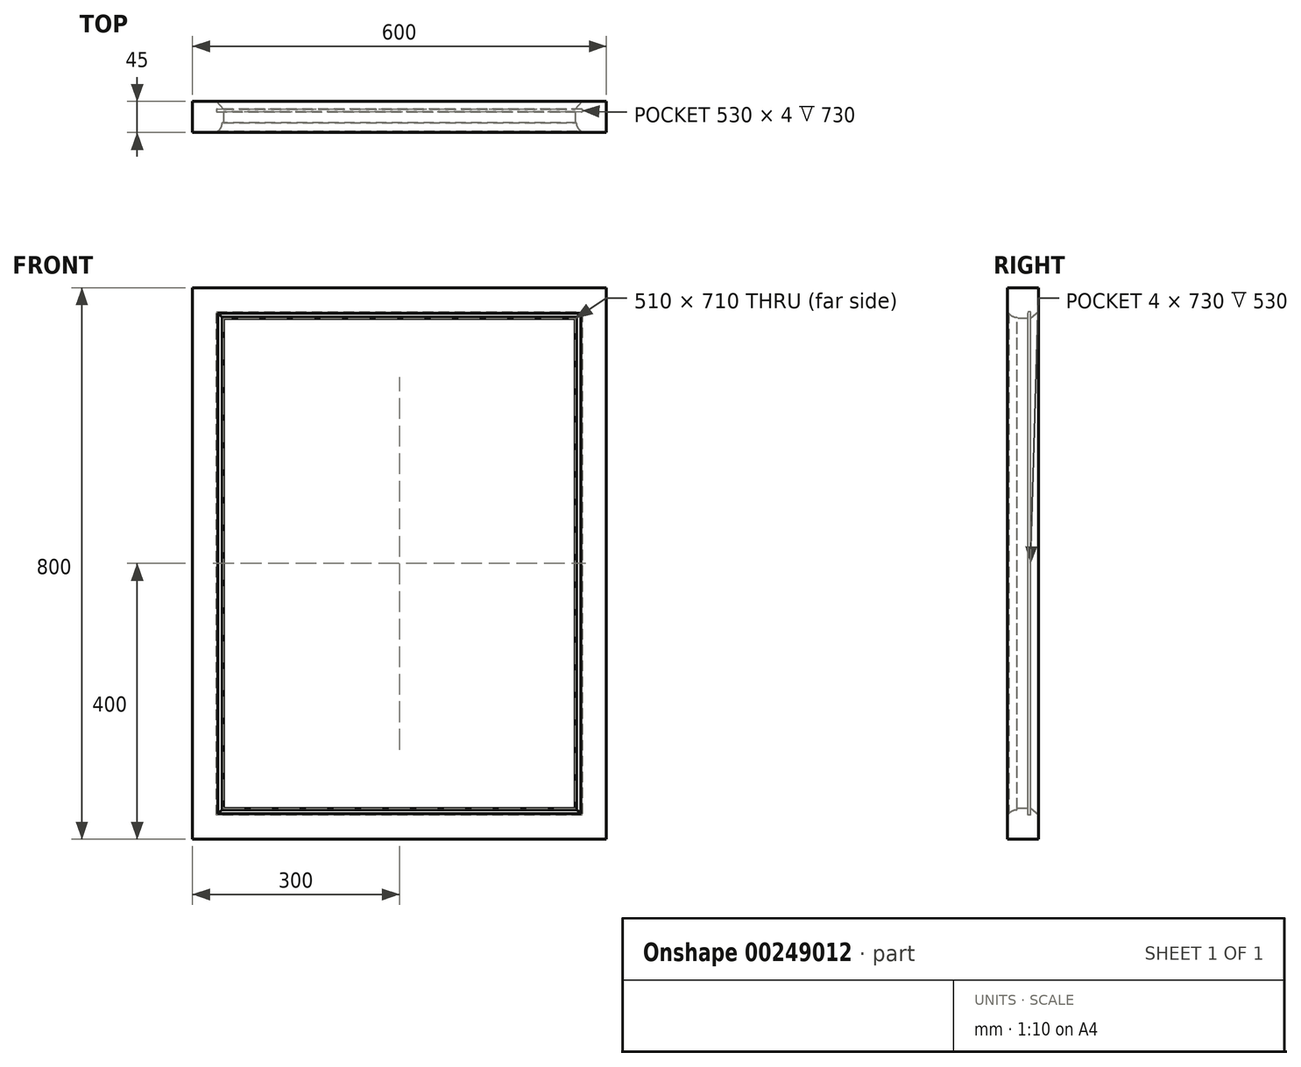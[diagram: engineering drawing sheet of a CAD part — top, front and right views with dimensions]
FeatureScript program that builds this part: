
annotation { "Feature Type Name" : "Feature", "Feature Type Description" : "" }
export const myFeature = defineFeature(function(context is Context, id is Id, definition is map)
    precondition{}
    {
        {
            var Q0;
            Q0=qCreatedBy(makeId("Front.planeOp"),FACE);
            var sketch = newSketch(context, id + "F0", { "sketchPlane" : qUnion([Q0])});
            skLineSegment(sketch, "E0.bottom", {"start": v(300, 400) * mm, "end": v(-300, 400) * mm});
            skLineSegment(sketch, "E0.top", {"start": v(300, -400) * mm, "end": v(-300, -400) * mm});
            skLineSegment(sketch, "E0.left", {"start": v(300, 400) * mm, "end": v(300, -400) * mm});
            skLineSegment(sketch, "E0.right", {"start": v(-300, 400) * mm, "end": v(-300, -400) * mm});
            skPoint(sketch, "E0.middle", {"position": v(0, 0) * mm});
            skSolve(sketch);
        }
        {
            var Q0;
            Q0=qCreatedBy(makeId("Top.planeOp"),FACE);
            var sketch = newSketch(context, id + "F1", { "sketchPlane" : qUnion([Q0])});
            skLineSegment(sketch, "E1", {"start": v(0, 0) * mm, "end": v(-300, 0) * mm, "construction": true});
            skLineSegment(sketch, "E2.left", {"start": v(-300, 0) * mm, "end": v(-300, -45) * mm, "construction": true});
            skLineSegment(sketch, "E3", {"start": v(-300, 0) * mm, "end": v(-300, -45) * mm});
            skLineSegment(sketch, "E4", {"start": v(-300, 0) * mm, "end": v(-265, 0) * mm});
            skLineSegment(sketch, "E5", {"start": v(-265, 0) * mm, "end": v(-255, -11) * mm});
            skLineSegment(sketch, "E6", {"start": v(-255, -11) * mm, "end": v(-265, -11) * mm});
            skLineSegment(sketch, "E7", {"start": v(-265, -11) * mm, "end": v(-265, -15) * mm});
            skLineSegment(sketch, "E8", {"start": v(-265, -15) * mm, "end": v(-255, -15) * mm});
            skLineSegment(sketch, "E9", {"start": v(-263, -43) * mm, "end": v(-263, -45) * mm});
            skLineSegment(sketch, "E10", {"start": v(-263, -45) * mm, "end": v(-300, -45) * mm});
            skLineSegment(sketch, "E11", {"start": v(-255, -31) * mm, "end": v(-257, -31) * mm});
            skLineSegment(sketch, "E12", {"start": v(-255, -15) * mm, "end": v(-255, -31) * mm});
            skLineSegment(sketch, "E13", {"start": v(-257, -31) * mm, "end": v(-300, -31) * mm, "construction": true});
            skArc(sketch, "E14", {"start": v(-263, -43) * mm, "mid": v(-258.58, -37.7) * mm, "end": v(-257, -31) * mm});
            skSolve(sketch);
        }
        {
            var Q0;
            Q0=makeQuery(id+"F1.imprint","IMPRINT",FACE,{"disambiguationData":[TD([[makeQuery(id+"F1.imprint","IMPRINT",EDGE,{"derivedFrom":sQuery(id+"F1.wireOp",EDGE,"E3")}),1.0]])]});
            var Q1;
            Q1=sQuery(id+"F0.wireOp",EDGE,"E0.bottom");
            var Q2;
            Q2=sQuery(id+"F0.wireOp",EDGE,"E0.right");
            var Q3;
            Q3=sQuery(id+"F0.wireOp",EDGE,"E0.top");
            var Q4;
            Q4=sQuery(id+"F0.wireOp",EDGE,"E0.left");
            sweep(context, id + "F2", {"profiles" : qUnion([Q0]), "path" : qUnion([Q1, Q2, Q3, Q4])});
        }
    });
